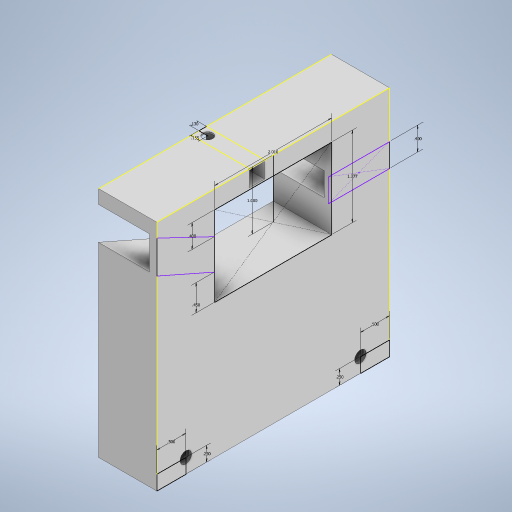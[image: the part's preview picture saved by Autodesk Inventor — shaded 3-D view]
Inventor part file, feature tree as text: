
AUTODESK INVENTOR PART (.ipt)
format: ipt  version: 2024.1 (Build 281209000, 209)  size: 313,344 bytes
history: native  units: in
note: dims shown in document units (in); Inventor stores cm internally (conversion verified against a paired STEP export)
features: sketch x6, extrude x4, hole x3
ambient origin geometry x8: Origin, YZ Plane, XZ Plane, XY Plane, X Axis, Y Axis, Z Axis, Center Point
bodies: Solid1 (feature_tree)
feature tree (13):
  extrude  "Extrusion1"  Depth=4.0in
  sketch  "Sketch2"  dims[d2=1.0in d3=0.0in d4=0.5in]
  extrude  "Extrusion2"  Depth=1.0in
  hole  "Hole1"  [1 undecoded]
  extrude  "Extrusion4"  Depth=1.0in
  extrude  "Extrusion5"  Depth=1.377in
  sketch  "Sketch7"  dims[d9=2.01in d10=1.377in]
  hole  "Hole2"  [1 undecoded]
  hole  "Hole3"  [1 undecoded]
  sketch  "Sketch1"  dims[d0=4.0in d1=4.0in]
  sketch  "Sketch5"  dims[d5=0.25in d6=0.5in]
  sketch  "Sketch6"  dims[d7=0.25in d8=1.0in]
  sketch  "Sketch8"  dims[d11=1.0in d12=0.0in d13=0.196in d14=1.0in d15=0.375in d16=0.25in d17=0.5635in d18=1.0in d19=0.8108in d20=0.4in d21=0.4in d22=0.45in d28=0.125in d29=0.0in d30=0.277in d31=0.156in d32=0.26in d33=0.26in d34=1.0in d35=0.0in d36=0.13in d37=0.1551in d38=0.17in d39=0.75in d40=0.281in d41=0.138in d42=0.5635in d43=0.25in d44=0.8108in d45=0.104in d46=0.125in d47=0.375in d48=0.25in d49=0.5635in d50=0.432in d51=0.8108in]
note: 3 required parameter values undecoded (feature->parameter linkage not recoverable at this tier; creation-order binding heuristic only, values carry confidence <= 0.55)
